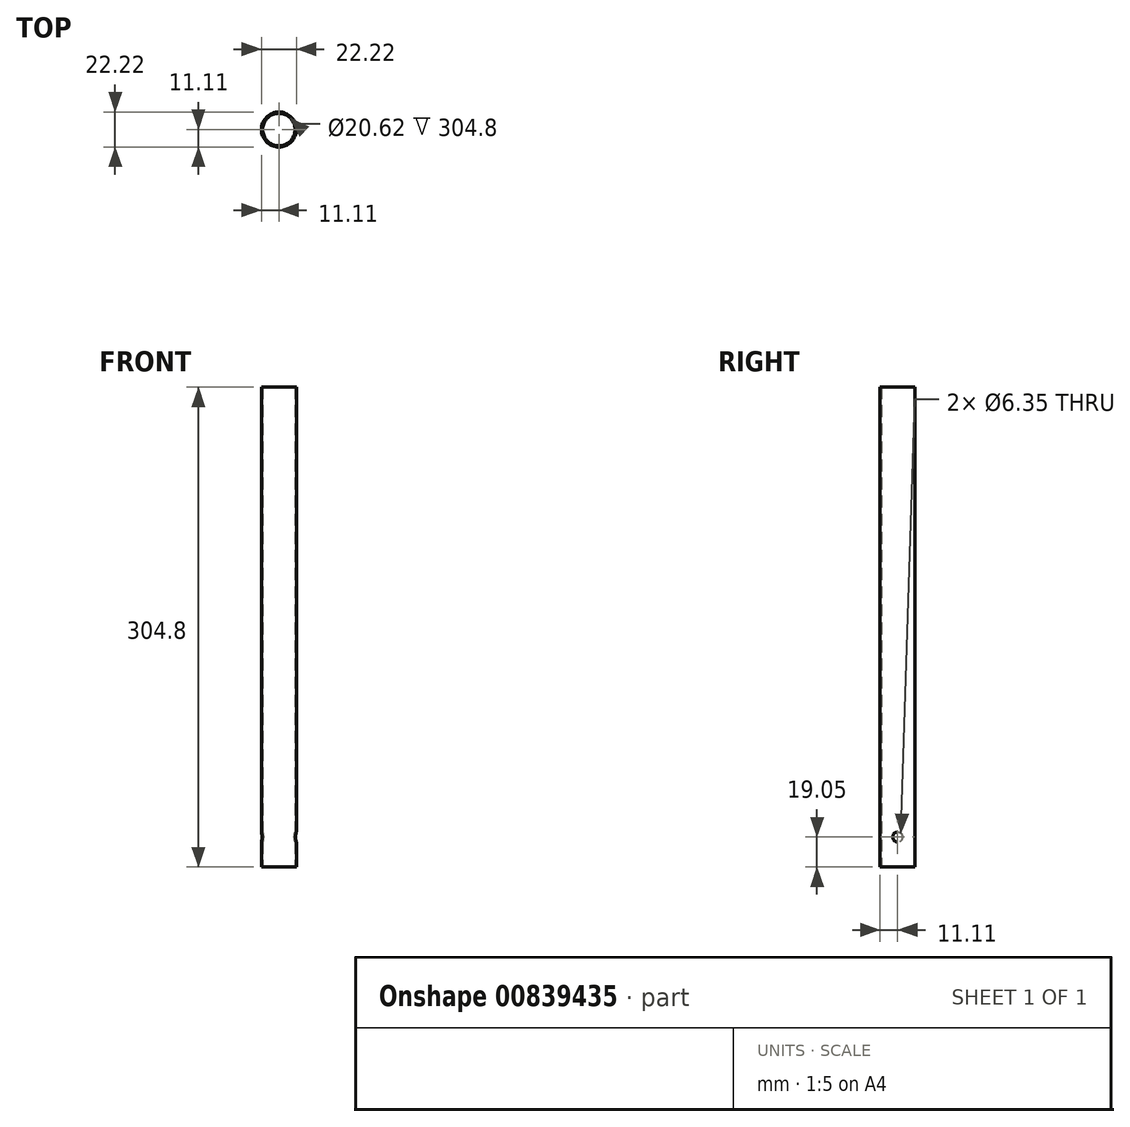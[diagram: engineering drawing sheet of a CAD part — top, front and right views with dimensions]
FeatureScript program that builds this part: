
annotation { "Feature Type Name" : "Feature", "Feature Type Description" : "" }
export const myFeature = defineFeature(function(context is Context, id is Id, definition is map)
    precondition{}
    {
        {
            var Q0;
            Q0=qCreatedBy(makeId("Top.planeOp"),FACE);
            var sketch = newSketch(context, id + "F0", { "sketchPlane" : qUnion([Q0])});
            skCircle(sketch, "E0", {"center": v(0, 0) * mm, "radius": 11.11 * mm});
            skCircle(sketch, "E1", {"center": v(0, 0) * mm, "radius": 10.31 * mm});
            skSolve(sketch);
        }
        {
            var Q0;
            Q0 = qSketchRegion(id + "F0", true);
            extrude(context, id + "F1", {"entities" : qUnion([Q0]), "depth" : 304.8 * mm, "offsetDistance" : 25.4 * mm});
        }
        {
            var Q0;
            Q0=qCreatedBy(makeId("Right.planeOp"),FACE);
            var sketch = newSketch(context, id + "F2", { "sketchPlane" : qUnion([Q0])});
            skCircle(sketch, "E2", {"center": v(0, 19.05) * mm, "radius": 3.18 * mm});
            skSolve(sketch);
        }
        {
            var Q0;
            Q0 = qSketchRegion(id + "F2", true);
            extrude(context, id + "F3", {"entities" : qUnion([Q0]), "operationType" : NewBodyOperationType.REMOVE, "endBound" : BoundingType.THROUGH_ALL, "oppositeDirection" : true, "depth" : 25.4 * mm, "offsetDistance" : 25.4 * mm, "hasSecondDirection" : true, "secondDirectionBound" : BoundingType.THROUGH_ALL, "secondDirectionOppositeDirection" : false, "secondDirectionDepth" : 25.4 * mm});
        }
    });
